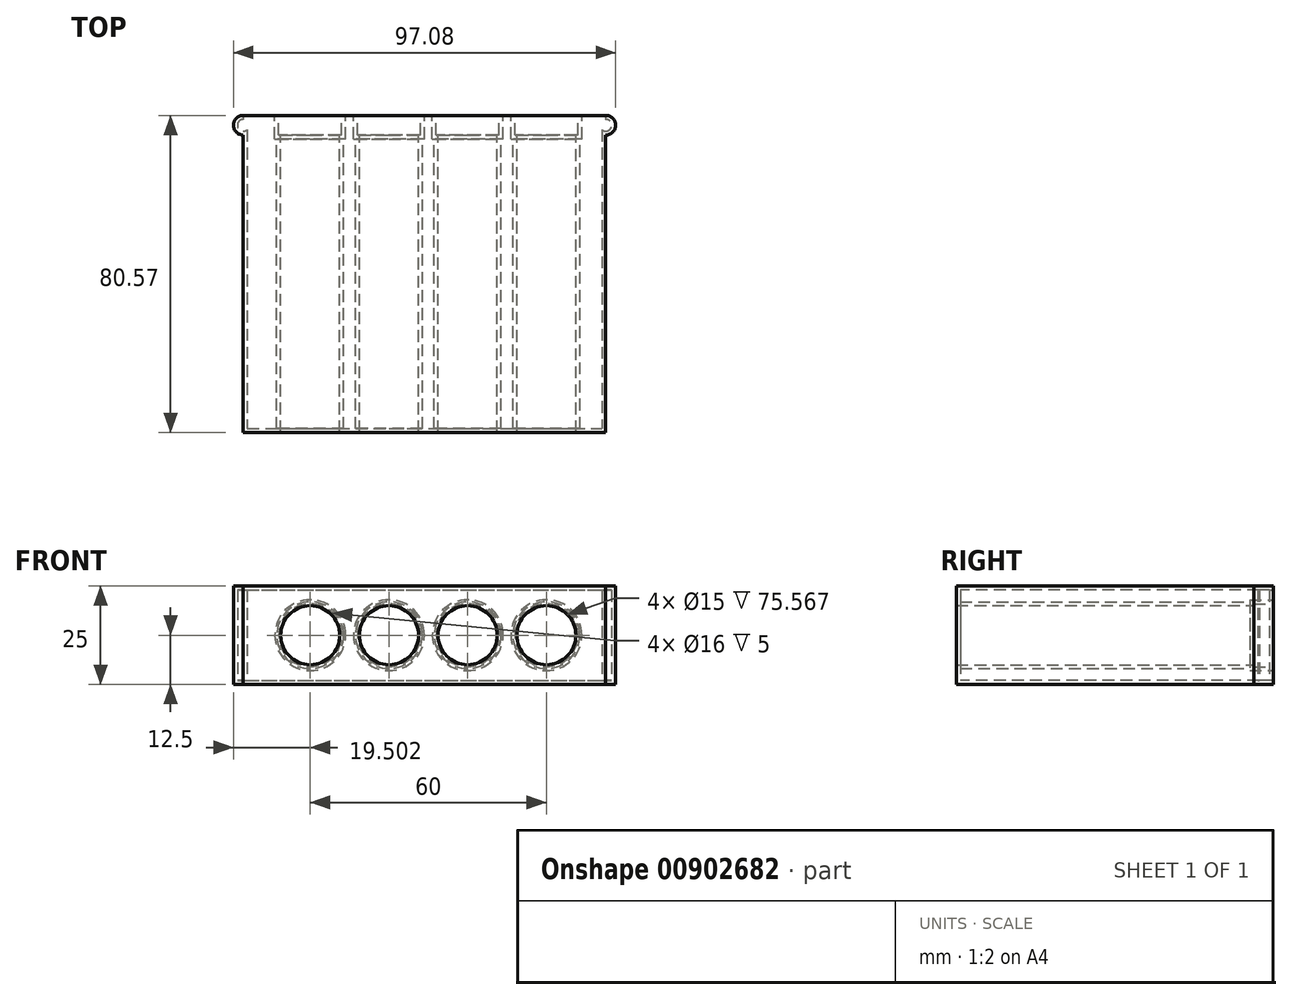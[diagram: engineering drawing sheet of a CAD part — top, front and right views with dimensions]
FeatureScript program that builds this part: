
annotation { "Feature Type Name" : "Feature", "Feature Type Description" : "" }
export const myFeature = defineFeature(function(context is Context, id is Id, definition is map)
    precondition{}
    {
        {
            var Q0;
            Q0=qCreatedBy(makeId("Top.planeOp"),FACE);
            var sketch = newSketch(context, id + "F0", { "sketchPlane" : qUnion([Q0])});
            skLineSegment(sketch, "E0.bottom", {"start": v(-40.7, 36.57) * mm, "end": v(51.38, 36.57) * mm});
            skLineSegment(sketch, "E0.top", {"start": v(-40.7, -41.5) * mm, "end": v(51.38, -41.5) * mm});
            skLineSegment(sketch, "E0.left", {"start": v(-40.7, 36.57) * mm, "end": v(-40.7, -41.5) * mm});
            skLineSegment(sketch, "E0.right", {"start": v(51.38, 36.57) * mm, "end": v(51.38, -41.5) * mm});
            skArc(sketch, "E1.0.startCap", {"start": v(-40.7, 34.07) * mm, "mid": v(-43.2, 36.57) * mm, "end": v(-40.7, 39.07) * mm});
            skArc(sketch, "E1.0.endCap", {"start": v(51.38, 39.07) * mm, "mid": v(53.88, 36.57) * mm, "end": v(51.38, 34.07) * mm});
            skLineSegment(sketch, "E1.0.left", {"start": v(-40.7, 39.07) * mm, "end": v(51.38, 39.07) * mm});
            skLineSegment(sketch, "E1.0.right", {"start": v(-40.7, 34.07) * mm, "end": v(51.38, 34.07) * mm});
            skSolve(sketch);
        }
        {
            var Q0;
            Q0 = qSketchRegion(id + "F0", true);
            extrude(context, id + "F1", {"entities" : qUnion([Q0]), "depth" : 25 * mm, "offsetDistance" : 25 * mm});
        }
        {
            var Q0;
            Q0=makeQuery(id+"F1.opExtrude","SWEPT_FACE",FACE,{"disambiguationData":[OSD([sQuery(id+"F0.wireOp",EDGE,"E1.0.left")])]});
            var sketch = newSketch(context, id + "F2", { "sketchPlane" : qUnion([Q0])});
            skCircle(sketch, "E2", {"center": v(23.7, 12.5) * mm, "radius": 7.5 * mm});
            skCircle(sketch, "E3", {"center": v(3.7, 12.5) * mm, "radius": 7.5 * mm});
            skCircle(sketch, "E4", {"center": v(-16.3, 12.5) * mm, "radius": 7.5 * mm});
            skCircle(sketch, "E5", {"center": v(-36.3, 12.5) * mm, "radius": 7.5 * mm});
            skSolve(sketch);
        }
        {
            var Q0;
            Q0=sQuery(id+"F2.wireOp",VERTEX,"E2.center");
            var Q1;
            Q1=sQuery(id+"F2.wireOp",VERTEX,"E4.center");
            var Q2;
            Q2=sQuery(id+"F2.wireOp",VERTEX,"E5.center");
            var Q3;
            Q3=sQuery(id+"F2.wireOp",VERTEX,"E3.center");
            var Q4;
            Q4=makeQuery(id+"F1.opExtrude","SWEPT_BODY",BODY,{"disambiguationData":[OSD([sQuery(id+"F0.wireOp",EDGE,"E0.top"),sQuery(id+"F0.wireOp",EDGE,"E0.left"),sQuery(id+"F0.wireOp",EDGE,"E0.right"),sQuery(id+"F0.wireOp",EDGE,"E1.0.startCap"),sQuery(id+"F0.wireOp",EDGE,"E1.0.endCap"),sQuery(id+"F0.wireOp",EDGE,"E1.0.left")])]});
            hole(context, id + "F3", {"style" : HoleStyle.C_BORE, "endStyle" : HoleEndStyle.THROUGH, "holeDiameter" : 15 * mm, "cBoreDiameter" : 16 * mm, "cBoreDepth" : 5 * mm, "majorDiameter" : 5 * mm, "isTappedThrough" : true, "tappedDepth" : 12 * mm, "tapClearance" : 3, "startFromSketch" : true, "locations" : qUnion([Q0, Q1, Q2, Q3]), "scope" : qUnion([Q4])});
        }
        {
            var Q0;
            Q0=makeQuery(id+"F1.opExtrude","SWEPT_FACE",FACE,{"disambiguationData":[OSD([sQuery(id+"F0.wireOp",EDGE,"E1.0.left")])]});
            shell(context, id + "F4", {"entities" : qUnion([Q0]), "thickness" : 1 * mm});
        }
    });
